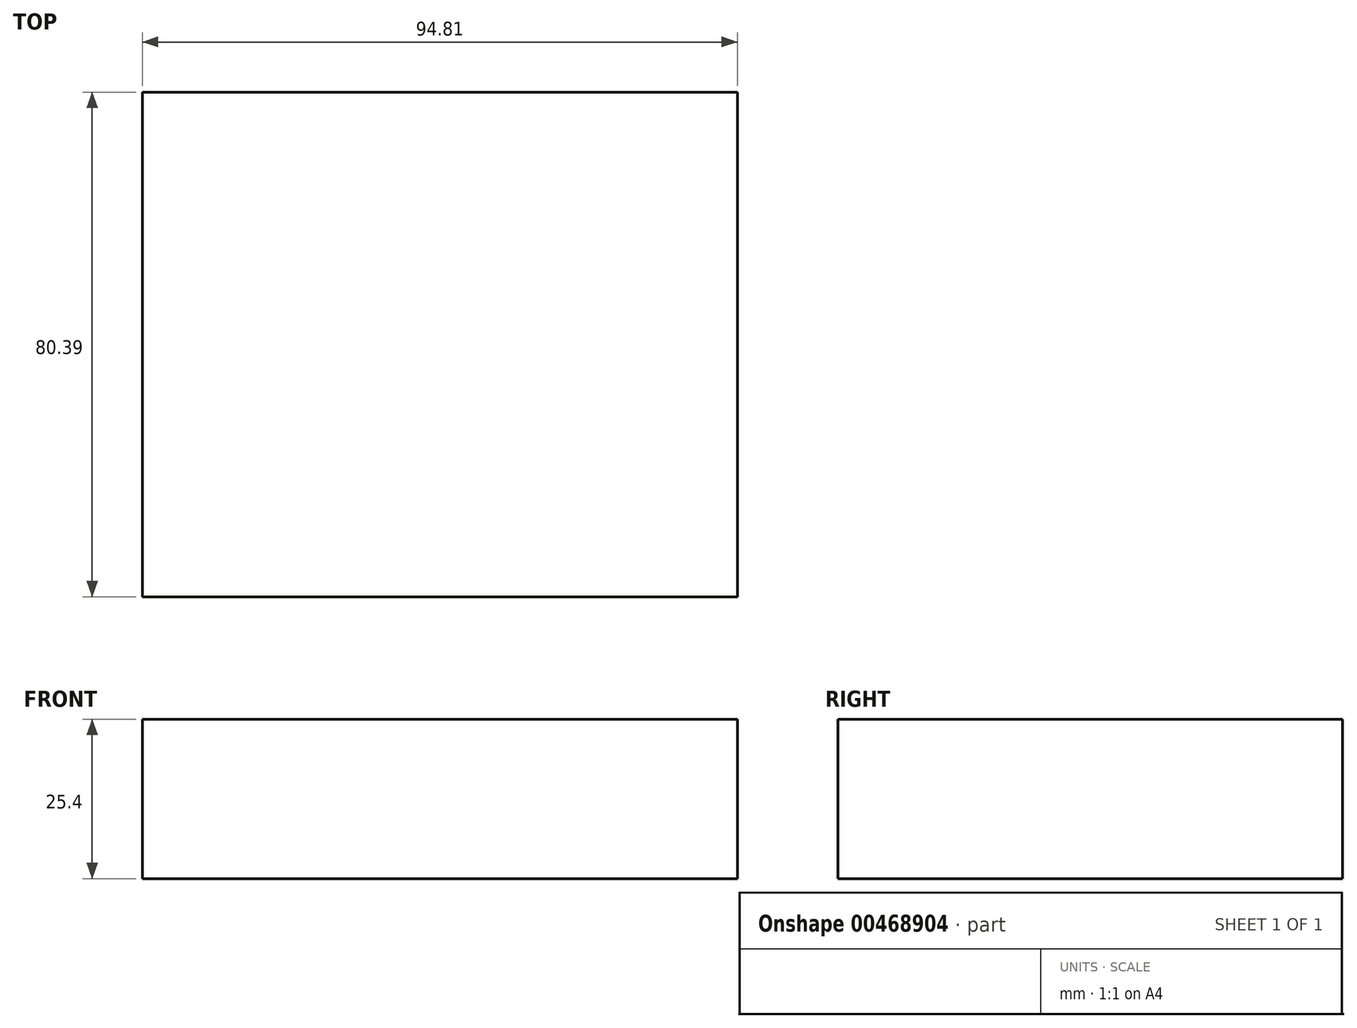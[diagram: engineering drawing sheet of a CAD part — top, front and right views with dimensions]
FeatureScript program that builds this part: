
annotation { "Feature Type Name" : "Feature", "Feature Type Description" : "" }
export const myFeature = defineFeature(function(context is Context, id is Id, definition is map)
    precondition{}
    {
        {
            var Q0;
            Q0=qCreatedBy(makeId("Top.planeOp"),FACE);
            var sketch = newSketch(context, id + "F0", { "sketchPlane" : qUnion([Q0])});
            skLineSegment(sketch, "E0.bottom", {"start": v(0, 0) * mm, "end": v(94.81, 0) * mm});
            skLineSegment(sketch, "E0.top", {"start": v(0, 80.39) * mm, "end": v(94.81, 80.39) * mm});
            skLineSegment(sketch, "E0.left", {"start": v(0, 0) * mm, "end": v(0, 80.39) * mm});
            skLineSegment(sketch, "E0.right", {"start": v(94.81, 0) * mm, "end": v(94.81, 80.39) * mm});
            skSolve(sketch);
        }
        {
            var Q0;
            Q0=makeQuery(id+"F0.imprint","IMPRINT",FACE,{"disambiguationData":[TD([[makeQuery(id+"F0.imprint","IMPRINT",EDGE,{"derivedFrom":sQuery(id+"F0.wireOp",EDGE,"E0.bottom")}),1.0]])]});
            extrude(context, id + "F1", {"entities" : qUnion([Q0]), "depth" : 25.4 * mm, "offsetDistance" : 25.4 * mm});
        }
    });
